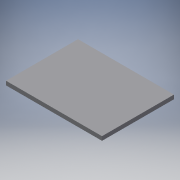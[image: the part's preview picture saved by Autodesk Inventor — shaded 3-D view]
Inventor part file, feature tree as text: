
AUTODESK INVENTOR PART (.ipt)
format: ipt  version: 2017 (Build 210142000, 142)  size: 88,064 bytes
history: native  units: in
note: dims shown in document units (in); Inventor stores cm internally (conversion verified against a paired STEP export)
features: extrude x1, sketch x1
ambient origin geometry x8: Origin, YZ Plane, XZ Plane, XY Plane, X Axis, Y Axis, Z Axis, Center Point
bodies: Solid1 (feature_tree)
feature tree (2):
  extrude  "Extrusion1"  Depth=48.0in
  sketch  "Sketch1"  dims[d0=36.0in d1=48.0in d2=2.0in d3=0.0in]
